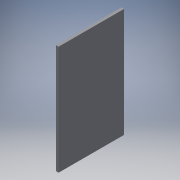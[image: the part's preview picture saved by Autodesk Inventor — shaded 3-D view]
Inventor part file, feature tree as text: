
AUTODESK INVENTOR PART (.ipt)
format: ipt  version: 2016 (Build 200138000, 138)  size: 98,816 bytes
history: native  units: in
note: dims shown in document units (in); Inventor stores cm internally (conversion verified against a paired STEP export)
features: extrude x2, sketch x2
ambient origin geometry x8: Origin, YZ Plane, XZ Plane, XY Plane, X Axis, Y Axis, Z Axis, Center Point
bodies: Solid1 (feature_tree)
feature tree (4):
  extrude  "Extrusion1"  Depth=3.0in
  extrude  "Extrusion2"  Depth=0.125in
  sketch  "Sketch1"  dims[d0=6.75in d1=3.0in]
  sketch  "Sketch2"  dims[d2=0.125in d3=0.0in d4=0.2656in d5=1.211in d6=1.5in d7=0.2656in d8=1.5in d9=1.4142in d10=0.125in d11=0.0in]
